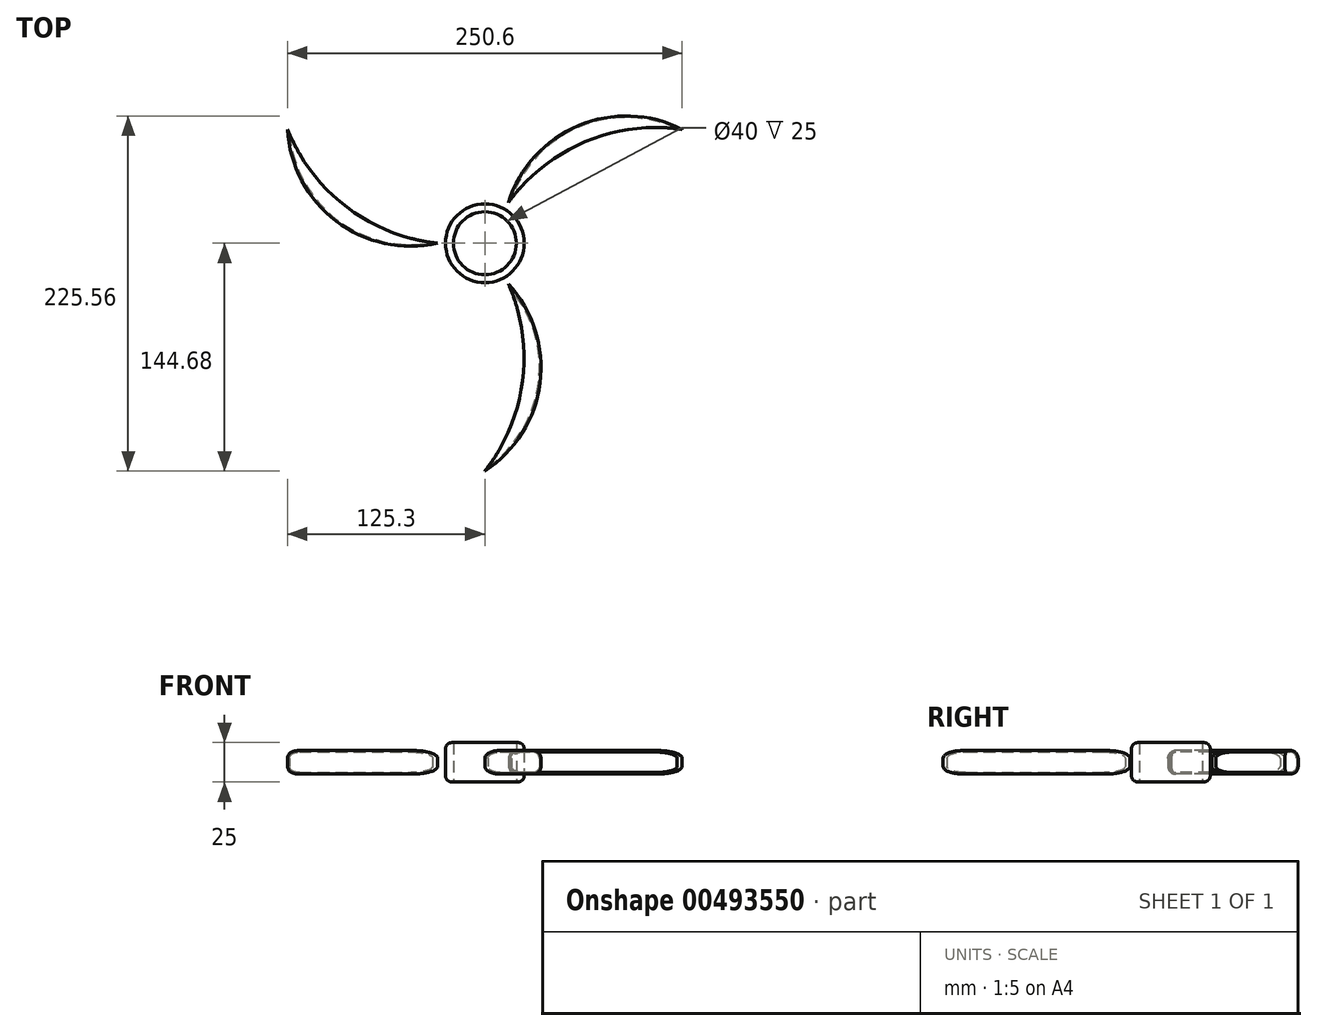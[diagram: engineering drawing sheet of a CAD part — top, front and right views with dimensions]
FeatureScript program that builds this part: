
annotation { "Feature Type Name" : "Feature", "Feature Type Description" : "" }
export const myFeature = defineFeature(function(context is Context, id is Id, definition is map)
    precondition{}
    {
        {
            var Q0;
            Q0=qCreatedBy(makeId("Top.planeOp"),FACE);
            var sketch = newSketch(context, id + "F0", { "sketchPlane" : qUnion([Q0])});
            skPoint(sketch, "E0.0.midPoint", {"position": v(0, 30) * mm});
            skArc(sketch, "E1", {"start": v(-125.3, 72.34) * mm, "mid": v(-87.68, 22.96) * mm, "end": v(-30, 0) * mm});
            skArc(sketch, "E2", {"start": v(-125.3, 72.34) * mm, "mid": v(-94.44, 14.05) * mm, "end": v(-30, 0) * mm});
            skArc(sketch, "E3.1.0", {"start": v(0, -144.68) * mm, "mid": v(23.95, -87.41) * mm, "end": v(15, -25.98) * mm});
            skArc(sketch, "E3.1.1", {"start": v(0, -144.68) * mm, "mid": v(35.05, -88.81) * mm, "end": v(15, -25.98) * mm});
            skArc(sketch, "E3.2.0", {"start": v(125.3, 72.34) * mm, "mid": v(63.72, 64.45) * mm, "end": v(15, 25.98) * mm});
            skArc(sketch, "E3.2.1", {"start": v(125.3, 72.34) * mm, "mid": v(59.39, 74.76) * mm, "end": v(15, 25.98) * mm});
            skPoint(sketch, "E3.center", {"position": v(0, 0) * mm});
            skSolve(sketch);
        }
        {
            var Q0;
            Q0 = qSketchRegion(id + "F0", true);
            extrude(context, id + "F1", {"entities" : qUnion([Q0]), "endBound" : BoundingType.SYMMETRIC, "depth" : 15 * mm, "offsetDistance" : 25 * mm});
        }
        {
            var Q0;
            Q0=makeQuery(id+"F1.opExtrude","CAP_EDGE",EDGE,{"disambiguationData":[OSD([sQuery(id+"F0.wireOp",EDGE,"E3.1.1")])],"isStart":false});
            var Q1;
            Q1=makeQuery(id+"F1.opExtrude","CAP_EDGE",EDGE,{"disambiguationData":[OSD([sQuery(id+"F0.wireOp",EDGE,"E3.1.1")])],"isStart":true});
            var Q2;
            Q2=makeQuery(id+"F1.opExtrude","CAP_EDGE",EDGE,{"disambiguationData":[OSD([sQuery(id+"F0.wireOp",EDGE,"E2")])],"isStart":false});
            var Q3;
            Q3=makeQuery(id+"F1.opExtrude","CAP_EDGE",EDGE,{"disambiguationData":[OSD([sQuery(id+"F0.wireOp",EDGE,"E3.2.1")])],"isStart":false});
            var Q4;
            Q4=makeQuery(id+"F1.opExtrude","CAP_EDGE",EDGE,{"disambiguationData":[OSD([sQuery(id+"F0.wireOp",EDGE,"E3.2.1")])],"isStart":true});
            var Q5;
            Q5=makeQuery(id+"F1.opExtrude","CAP_EDGE",EDGE,{"disambiguationData":[OSD([sQuery(id+"F0.wireOp",EDGE,"E2")])],"isStart":true});
            fillet(context, id + "F2", {"entities" : qUnion([Q0, Q1, Q2, Q3, Q4, Q5]), "radius" : 5 * mm, "tangentPropagation" : true, "allowEdgeOverflow" : false});
        }
        {
            var Q0;
            Q0=makeQuery(id+"F1.opExtrude","SWEPT_FACE",FACE,{"disambiguationData":[OSD([sQuery(id+"F0.wireOp",EDGE,"E3.1.0")])]});
            shell(context, id + "F3", {"entities" : qUnion([Q0]), "thickness" : 1 * mm});
        }
        {
            var Q0;
            Q0=makeQuery(id+"F1.opExtrude","SWEPT_FACE",FACE,{"disambiguationData":[OSD([sQuery(id+"F0.wireOp",EDGE,"E1")])]});
            var Q1;
            Q1=makeQuery(id+"F1.opExtrude","SWEPT_FACE",FACE,{"disambiguationData":[OSD([sQuery(id+"F0.wireOp",EDGE,"E3.2.0")])]});
            shell(context, id + "F4", {"entities" : qUnion([Q0, Q1]), "thickness" : 1 * mm});
        }
        {
            var Q0;
            Q0=qCreatedBy(makeId("Top.planeOp"),FACE);
            var sketch = newSketch(context, id + "F5", { "sketchPlane" : qUnion([Q0])});
            skCircle(sketch, "E4", {"center": v(0, 0) * mm, "radius": 20 * mm});
            skCircle(sketch, "E5", {"center": v(0, 0) * mm, "radius": 25 * mm});
            skSolve(sketch);
        }
        {
            var Q0;
            Q0 = qSketchRegion(id + "F5", true);
            extrude(context, id + "F6", {"entities" : qUnion([Q0]), "endBound" : BoundingType.SYMMETRIC, "depth" : 25 * mm, "offsetDistance" : 25 * mm});
        }
        {
            var Q0;
            Q0=makeQuery(id+"F6.opExtrude","CAP_EDGE",EDGE,{"disambiguationData":[OSD([sQuery(id+"F5.wireOp",EDGE,"E5")])],"isStart":false});
            var Q1;
            Q1=makeQuery(id+"F6.opExtrude","CAP_EDGE",EDGE,{"disambiguationData":[OSD([sQuery(id+"F5.wireOp",EDGE,"E5")])],"isStart":true});
            fillet(context, id + "F7", {"entities" : qUnion([Q0, Q1]), "radius" : 4 * mm, "tangentPropagation" : true, "allowEdgeOverflow" : false});
        }
    });
